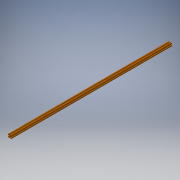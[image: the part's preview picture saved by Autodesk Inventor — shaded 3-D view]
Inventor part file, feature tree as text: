
AUTODESK INVENTOR PART (.ipt)
format: ipt  version: 2017 SP1 (Build 210196100, 196)  size: 233,472 bytes
history: native  units: in
note: dims shown in document units (in); Inventor stores cm internally (conversion verified against a paired STEP export)
features: extrude x1, pattern_circular x1, sketch x1
ambient origin geometry x8: Origin, YZ Plane, XZ Plane, XY Plane, X Axis, Y Axis, Z Axis, Center Point
bodies: Solid1 (feature_tree)
feature tree (3):
  extrude  "Extrusion1"  TaperAngle=45.0deg  [1 undecoded]
  pattern_circular  "Circular Pattern1"  [2 undecoded]
  sketch  "Sketch1"  dims[d0=0.16in d1=45.0deg d10=0.0312in d13=0.1015in d14=0.069in d21=0.061in d23=0.01in d24=0.115in d25=48.0in d26=0.0in d27=1.5748in d28=360.0deg d30=0.5in d32=0.375in d33=0.1875in d34=0.06in]
note: 3 required parameter values undecoded (feature->parameter linkage not recoverable at this tier; creation-order binding heuristic only, values carry confidence <= 0.55)
